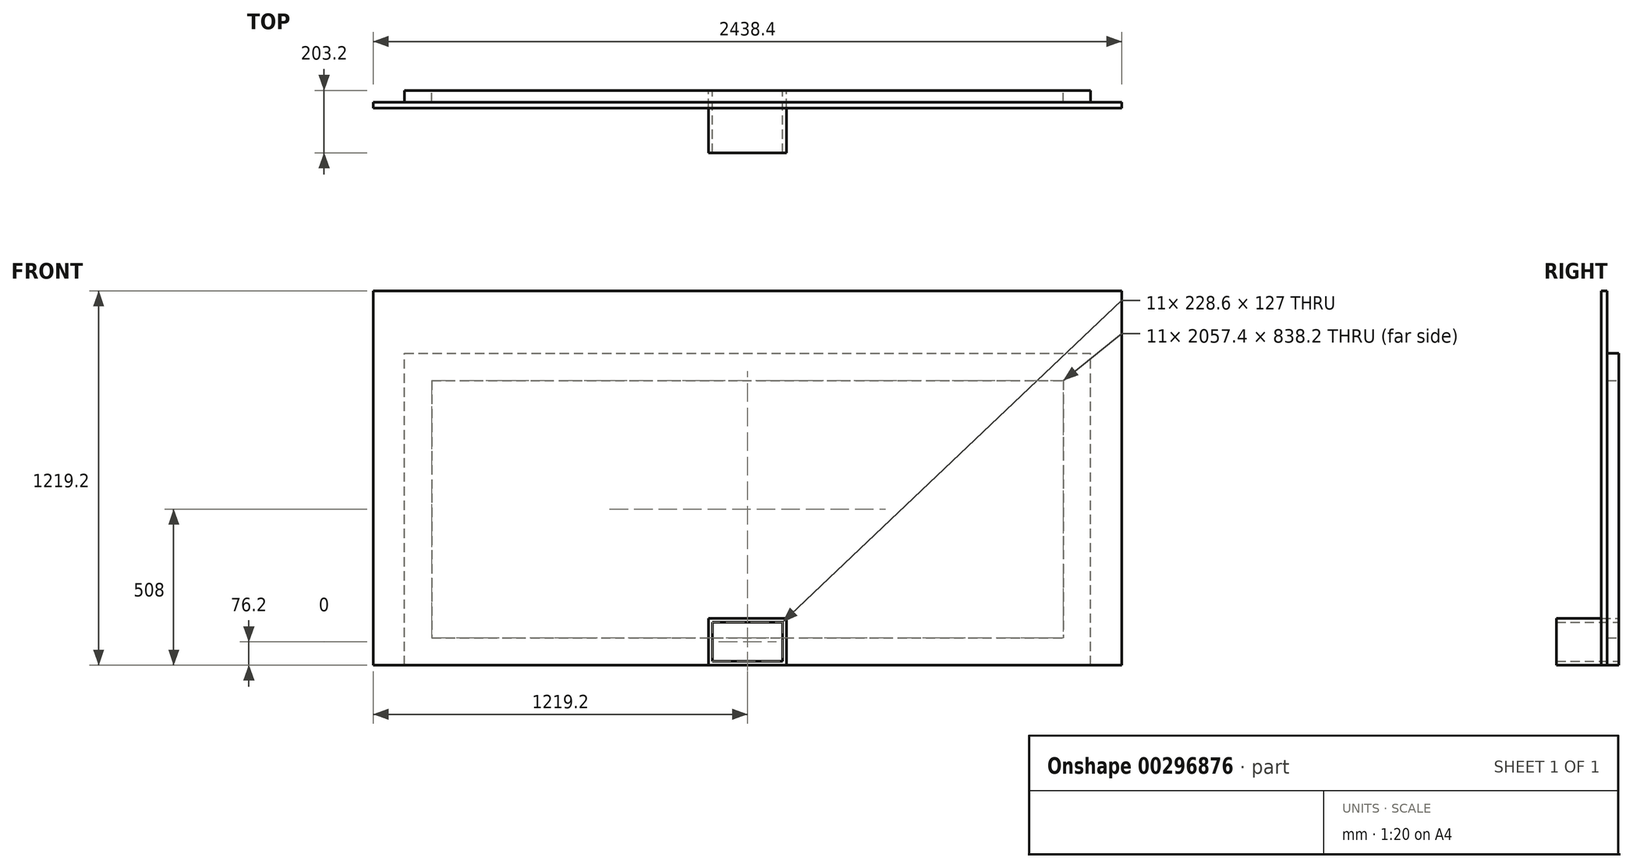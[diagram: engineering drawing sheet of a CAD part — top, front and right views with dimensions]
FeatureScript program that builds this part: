
annotation { "Feature Type Name" : "Feature", "Feature Type Description" : "" }
export const myFeature = defineFeature(function(context is Context, id is Id, definition is map)
    precondition{}
    {
        {
            var Q0;
            Q0=qCreatedBy(makeId("Front.planeOp"),FACE);
            var sketch = newSketch(context, id + "F0", { "sketchPlane" : qUnion([Q0])});
            skLineSegment(sketch, "E0.bottom", {"start": v(-1117.6, 0) * mm, "end": v(1117.6, 0) * mm});
            skLineSegment(sketch, "E0.top", {"start": v(-1117.6, 1016) * mm, "end": v(1117.6, 1016) * mm});
            skLineSegment(sketch, "E0.left", {"start": v(-1117.6, 0) * mm, "end": v(-1117.6, 1016) * mm});
            skLineSegment(sketch, "E0.right", {"start": v(1117.6, 0) * mm, "end": v(1117.6, 1016) * mm});
            skLineSegment(sketch, "E1.bottom", {"start": v(-1028.7, 927.1) * mm, "end": v(1028.7, 927.1) * mm});
            skLineSegment(sketch, "E1.top", {"start": v(-1028.7, 88.9) * mm, "end": v(1028.7, 88.9) * mm});
            skLineSegment(sketch, "E1.left", {"start": v(-1028.7, 927.1) * mm, "end": v(-1028.7, 88.9) * mm});
            skLineSegment(sketch, "E1.right", {"start": v(1028.7, 927.1) * mm, "end": v(1028.7, 88.9) * mm});
            skLineSegment(sketch, "E2", {"start": v(0, 0) * mm, "end": v(0, 88.9) * mm});
            skLineSegment(sketch, "E3", {"start": v(-1028.7, 508) * mm, "end": v(-1117.6, 508) * mm, "construction": true});
            skSolve(sketch);
        }
        {
            var Q0;
            Q0=makeQuery(id+"F0.imprint","IMPRINT",FACE,{"disambiguationData":[TD([[makeQuery(id+"F0.imprint","IMPRINT",EDGE,{"derivedFrom":sQuery(id+"F0.wireOp",EDGE,"E0.top")}),-1.0]])]});
            extrude(context, id + "F1", {"entities" : qUnion([Q0]), "depth" : 38.1 * mm});
        }
        {
            var Q0;
            Q0=makeQuery(id+"F1.opExtrude","CAP_FACE",FACE,{"disambiguationData":[OSD([sQuery(id+"F0.wireOp",EDGE,"E0.bottom"),sQuery(id+"F0.wireOp",EDGE,"E0.top"),sQuery(id+"F0.wireOp",EDGE,"E0.left"),sQuery(id+"F0.wireOp",EDGE,"E0.right"),sQuery(id+"F0.wireOp",EDGE,"E1.bottom"),sQuery(id+"F0.wireOp",EDGE,"E1.top"),sQuery(id+"F0.wireOp",EDGE,"E1.left"),sQuery(id+"F0.wireOp",EDGE,"E1.right")])],"isStart":false});
            var sketch = newSketch(context, id + "F2", { "sketchPlane" : qUnion([Q0])});
            skLineSegment(sketch, "E4.bottom", {"start": v(-1219.2, 1219.2) * mm, "end": v(1219.2, 1219.2) * mm});
            skLineSegment(sketch, "E4.top", {"start": v(-1219.2, 0) * mm, "end": v(1219.2, 0) * mm});
            skLineSegment(sketch, "E4.left", {"start": v(-1219.2, 1219.2) * mm, "end": v(-1219.2, 0) * mm});
            skLineSegment(sketch, "E4.right", {"start": v(1219.2, 1219.2) * mm, "end": v(1219.2, 0) * mm});
            skSolve(sketch);
        }
        {
            var Q0;
            {var subQ0=sQuery(id+"F2.wireOp",EDGE,"E4.bottom");Q0=makeQuery(id+"F2.imprint","IMPRINT",FACE,{"disambiguationData":[TD([[makeQuery(id+"F2.imprint","IMPRINT",EDGE,{"derivedFrom":subQ0}),-1.0]])]});}
            var Q1;
            Q1 = qSketchRegion(id + "F2", true);
            extrude(context, id + "F3", {"entities" : qUnion([Q0, Q1]), "depth" : 19.05 * mm});
        }
        {
            var Q0;
            Q0=qCreatedBy(makeId("Front.planeOp"),FACE);
            var sketch = newSketch(context, id + "F4", { "sketchPlane" : qUnion([Q0])});
            skLineSegment(sketch, "E5.bottom", {"start": v(-127, 152.4) * mm, "end": v(127, 152.4) * mm});
            skLineSegment(sketch, "E5.top", {"start": v(-127, 0) * mm, "end": v(127, 0) * mm});
            skLineSegment(sketch, "E5.left", {"start": v(-127, 152.4) * mm, "end": v(-127, 0) * mm});
            skLineSegment(sketch, "E5.right", {"start": v(127, 152.4) * mm, "end": v(127, 0) * mm});
            skLineSegment(sketch, "E6.bottom", {"start": v(-114.3, 139.7) * mm, "end": v(114.3, 139.7) * mm});
            skLineSegment(sketch, "E6.top", {"start": v(-114.3, 12.7) * mm, "end": v(114.3, 12.7) * mm});
            skLineSegment(sketch, "E6.left", {"start": v(-114.3, 139.7) * mm, "end": v(-114.3, 12.7) * mm});
            skLineSegment(sketch, "E6.right", {"start": v(114.3, 139.7) * mm, "end": v(114.3, 12.7) * mm});
            skLineSegment(sketch, "E7", {"start": v(-114.3, 76.2) * mm, "end": v(-127, 76.2) * mm, "construction": true});
            skLineSegment(sketch, "E8", {"start": v(0, 0) * mm, "end": v(0, 12.7) * mm, "construction": true});
            skSolve(sketch);
        }
        {
            var Q0;
            Q0=makeQuery(id+"F4.imprint","IMPRINT",FACE,{"disambiguationData":[TD([[makeQuery(id+"F4.imprint","IMPRINT",EDGE,{"derivedFrom":sQuery(id+"F4.wireOp",EDGE,"E5.bottom")}),-1.0]])]});
            extrude(context, id + "F5", {"entities" : qUnion([Q0]), "depth" : 203.2 * mm});
        }
    });
